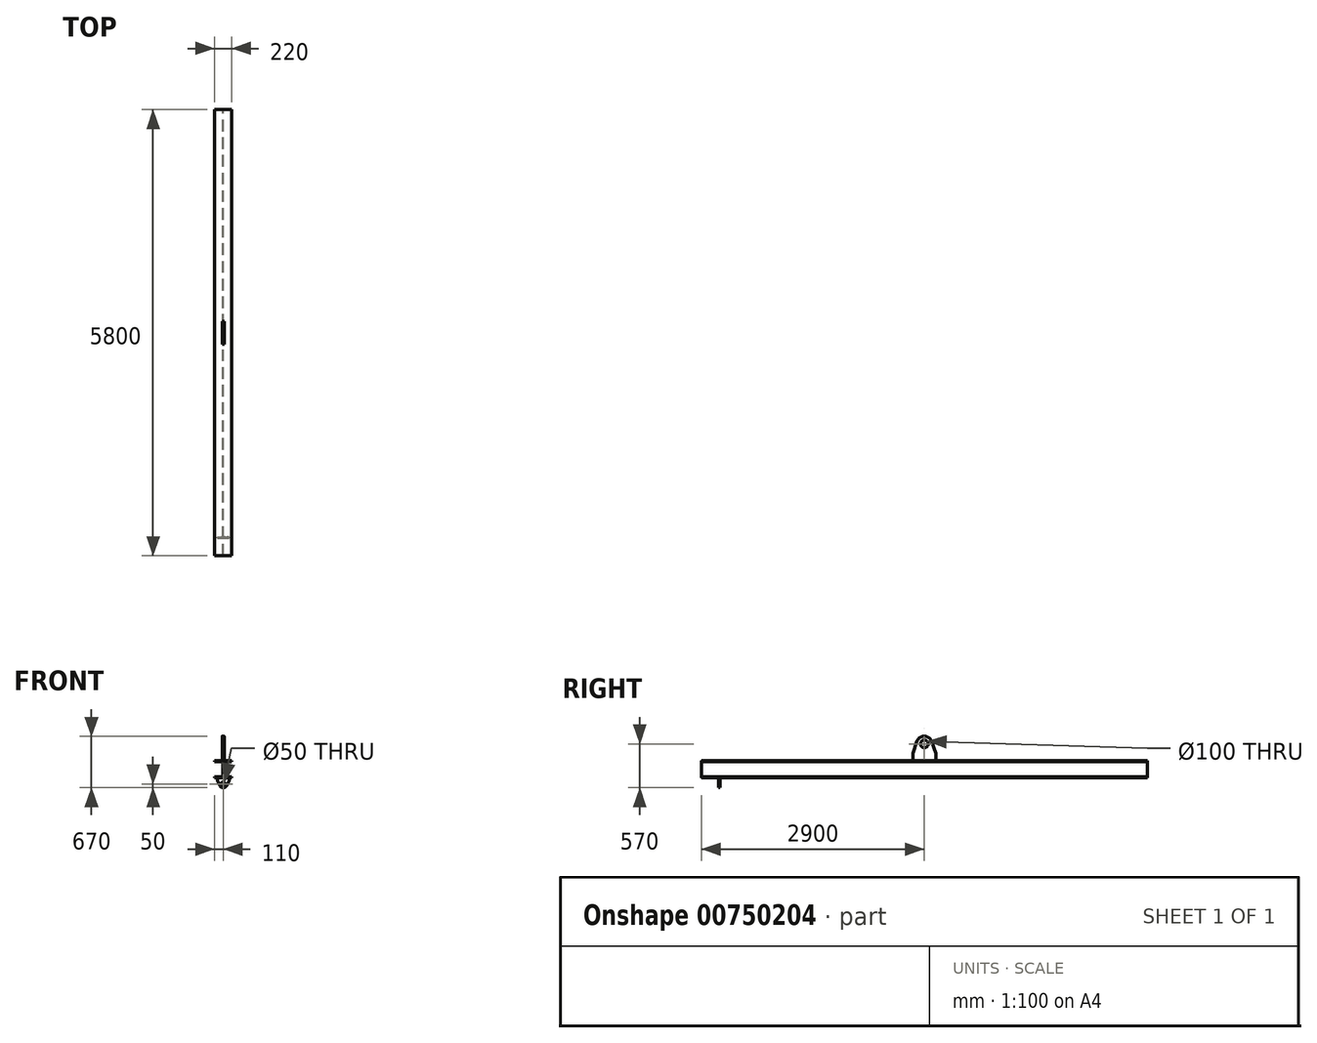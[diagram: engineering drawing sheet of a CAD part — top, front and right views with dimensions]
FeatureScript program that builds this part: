
annotation { "Feature Type Name" : "Feature", "Feature Type Description" : "" }
export const myFeature = defineFeature(function(context is Context, id is Id, definition is map)
    precondition{}
    {
        {
            var Q0;
            Q0=qCreatedBy(makeId("Front.planeOp"),FACE);
            var sketch = newSketch(context, id + "F0", { "sketchPlane" : qUnion([Q0])});
            skLineSegment(sketch, "E0", {"start": v(0, 0) * mm, "end": v(0, 110) * mm, "construction": true});
            skLineSegment(sketch, "E1", {"start": v(0, 0) * mm, "end": v(110, 0) * mm, "construction": true});
            skLineSegment(sketch, "E2", {"start": v(0, 110) * mm, "end": v(110, 110) * mm});
            skLineSegment(sketch, "E3", {"start": v(110, 110) * mm, "end": v(110, 100) * mm});
            skLineSegment(sketch, "E4", {"start": v(110, 100) * mm, "end": v(9, 100) * mm});
            skLineSegment(sketch, "E5", {"start": v(4, 95) * mm, "end": v(4, 0) * mm});
            skPoint(sketch, "E6.visualSharp", {"position": v(4, 100) * mm});
            skArc(sketch, "E6.filletArc", {"start": v(9, 100) * mm, "mid": v(5.46, 98.54) * mm, "end": v(4, 95) * mm});
            skLineSegment(sketch, "E7.MirrorCS", {"start": v(0, 110) * mm, "end": v(-110, 110) * mm});
            skLineSegment(sketch, "E8.MirrorCS", {"start": v(-110, 110) * mm, "end": v(-110, 100) * mm});
            skLineSegment(sketch, "E9.MirrorCS", {"start": v(-110, 100) * mm, "end": v(-9, 100) * mm});
            skArc(sketch, "E10.MirrorCS", {"start": v(-9, 100) * mm, "mid": v(-5.46, 98.54) * mm, "end": v(-4, 95) * mm});
            skLineSegment(sketch, "E11.MirrorCS", {"start": v(-4, 95) * mm, "end": v(-4, 0) * mm});
            skLineSegment(sketch, "E12.MirrorCS", {"start": v(110, -110) * mm, "end": v(110, -100) * mm});
            skLineSegment(sketch, "E13.MirrorCS", {"start": v(0, -110) * mm, "end": v(110, -110) * mm});
            skLineSegment(sketch, "E14.MirrorCS", {"start": v(110, -100) * mm, "end": v(9, -100) * mm});
            skArc(sketch, "E15.MirrorCS", {"start": v(9, -100) * mm, "mid": v(5.46, -98.54) * mm, "end": v(4, -95) * mm});
            skLineSegment(sketch, "E16.MirrorCS", {"start": v(4, -95) * mm, "end": v(4, 0) * mm});
            skLineSegment(sketch, "E17.MirrorCS", {"start": v(-4, -95) * mm, "end": v(-4, 0) * mm});
            skArc(sketch, "E18.MirrorCS", {"start": v(-9, -100) * mm, "mid": v(-5.46, -98.54) * mm, "end": v(-4, -95) * mm});
            skLineSegment(sketch, "E19.MirrorCS", {"start": v(-110, -100) * mm, "end": v(-9, -100) * mm});
            skLineSegment(sketch, "E20.MirrorCS", {"start": v(-110, -110) * mm, "end": v(-110, -100) * mm});
            skLineSegment(sketch, "E21.MirrorCS", {"start": v(0, -110) * mm, "end": v(-110, -110) * mm});
            skSolve(sketch);
        }
        {
            var Q0;
            Q0=makeQuery(id+"F0.imprint","IMPRINT",FACE,{"disambiguationData":[TD([[makeQuery(id+"F0.imprint","IMPRINT",EDGE,{"derivedFrom":sQuery(id+"F0.wireOp",EDGE,"E2")}),-1.0]])]});
            extrude(context, id + "F1", {"entities" : qUnion([Q0]), "endBound" : BoundingType.SYMMETRIC, "depth" : 5800 * mm, "offsetDistance" : 25 * mm});
        }
        {
            var Q0;
            Q0=qCreatedBy(makeId("Right.planeOp"),FACE);
            var sketch = newSketch(context, id + "F2", { "sketchPlane" : qUnion([Q0])});
            skLineSegment(sketch, "E22.bottom", {"start": v(-150, 210) * mm, "end": v(150, 210) * mm, "construction": true});
            skLineSegment(sketch, "E22.top", {"start": v(-150, 110) * mm, "end": v(150, 110) * mm});
            skLineSegment(sketch, "E22.left", {"start": v(-150, 210) * mm, "end": v(-150, 110) * mm});
            skLineSegment(sketch, "E22.right", {"start": v(150, 210) * mm, "end": v(150, 110) * mm});
            skCircle(sketch, "E23", {"center": v(0, 330) * mm, "radius": 50 * mm});
            skLineSegment(sketch, "E24", {"start": v(0, 0) * mm, "end": v(0, 628.46) * mm, "construction": true});
            skArc(sketch, "E25", {"start": v(93.99, 364.15) * mm, "mid": v(0, 430) * mm, "end": v(-93.99, 364.15) * mm});
            skLineSegment(sketch, "E26", {"start": v(-150, 210) * mm, "end": v(-93.99, 364.15) * mm});
            skLineSegment(sketch, "E27.MirrorCS", {"start": v(150, 210) * mm, "end": v(93.99, 364.15) * mm});
            skSolve(sketch);
        }
        {
            var Q0;
            Q0 = qSketchRegion(id + "F2", true);
            extrude(context, id + "F3", {"entities" : qUnion([Q0]), "operationType" : NewBodyOperationType.ADD, "endBound" : BoundingType.SYMMETRIC, "depth" : 25 * mm, "offsetDistance" : 25 * mm});
        }
        {
            var Q0;
            Q0=qCreatedBy(makeId("Front.planeOp"),FACE);
            cPlane(context, id + "F4", {"entities" : qUnion([Q0]), "cplaneType" : CPlaneType.OFFSET, "offset" : (5330 / 2) * mm, "width" : 150 * mm, "height" : 150 * mm});
        }
        {
            var Q0;
            Q0=qCreatedBy(id+"F4.planeOp",FACE);
            var sketch = newSketch(context, id + "F5", { "sketchPlane" : qUnion([Q0])});
            skLineSegment(sketch, "E28.bottom", {"start": v(-75, -110) * mm, "end": v(75, -110) * mm});
            skLineSegment(sketch, "E28.top", {"start": v(-75, -150) * mm, "end": v(75, -150) * mm, "construction": true});
            skLineSegment(sketch, "E28.left", {"start": v(-75, -110) * mm, "end": v(-75, -150) * mm});
            skLineSegment(sketch, "E28.right", {"start": v(75, -110) * mm, "end": v(75, -150) * mm});
            skCircle(sketch, "E29", {"center": v(0, -190) * mm, "radius": 25 * mm});
            skArc(sketch, "E30", {"start": v(-44.98, -211.84) * mm, "mid": v(0, -240) * mm, "end": v(44.98, -211.84) * mm});
            skLineSegment(sketch, "E31", {"start": v(-75, -150) * mm, "end": v(-44.98, -211.84) * mm});
            skLineSegment(sketch, "E32", {"start": v(75, -150) * mm, "end": v(44.98, -211.84) * mm});
            skSolve(sketch);
        }
        {
            var Q0;
            Q0 = qSketchRegion(id + "F5", true);
            extrude(context, id + "F6", {"entities" : qUnion([Q0]), "operationType" : NewBodyOperationType.ADD, "endBound" : BoundingType.SYMMETRIC, "depth" : 16 * mm, "offsetDistance" : 25 * mm});
        }
    });
